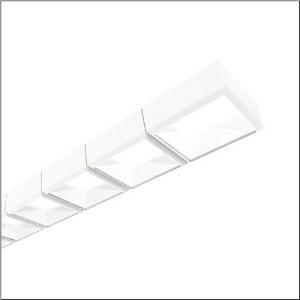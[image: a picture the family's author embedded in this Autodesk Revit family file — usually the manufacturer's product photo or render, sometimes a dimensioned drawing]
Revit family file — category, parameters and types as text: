
# Revit family: scriptus_r__11_5mz223d04wa_758a
name_source: partatom
category: Lighting Fixtures
units: mm (PartAtom-declared; Revit-internal decimal feet)

## family parameters
Cut with Voids When Loaded = No
Host = Face
Light Source = No
Part Type = Normal
Room Calculation Point = No
Round Connector Dimension = Use Diameter
Shared = No

## types (1)
- --- (1 x LED 4000K / CRI = 80 (unbekannt), 7230 lm, 4000K)
    Apparent Load = 51 VA
    CIE Flux Codes = 82 95 99 100 100
    Color Rendering = 80
    Color Temperature = 4000K
    Default Elevation = 1800 mm
    Description = Scriptus® 11, office luminaire, primary optical cover: lenses, CAT 2 (L<= 3000cd/m²), light emission: direct distribution, primary light characteristic: symmetric, installation type: surface-mounted, LED rated luminous flux: 7.230 lm, light colour: 840, colour temperature: 4000K, control gear: ECG DALI, with terminal, 5-pole, mains connection: 230V, AC, 50Hz, rated input power: 51W, housing, luminaire housing, of aluminium, traffic white (RAL 9016), length: 2.426 mm, width: 114 mm, height: 57mm, protection rating (complete): IP20, insulation class (complete): insulation class I (protective earthing), certification: CE, ENEC, VDE, protection symbol: F, permissible ambient temperature for indoor applications: 0..+35°C, standard: EN 50419, packaging unit: 1 piece
    Height = 57 mm
    Lamp = 1 x LED 4000K / CRI >= 80 (unbekannt)
    Lamp Light Flux = 7230 lm
    Lamp count = 1
    Length = 2426 mm
    Luminous efficacy = 143 lm/W
    Manufacturer = Siteco
    ModVariant = No
    Model = 5MZ223D04WA
    Mounting Place = Ceiling
    Mounting Type = Surface mounted
    Number of Poles = 1
    OnlyDefault = Yes
    Power Factor = 1
    Product Name = Scriptus® 11
    Product group = office luminaire | ceiling mounted
    ProductGroupID = 302
    Protection Class = Protection class I
    Protection Degree = IP 20
    RLX_Detail_Level = 1
    RlxData = <blob elided: 31293 chars, md5=bc968398>
    Socket = socket
    Standby Power = 0 W
    System Light Flux = 7230 lm
    System Power = 51 W
    Type Comments = factory setting: luminous flux: 100 % | dim-lin: 254 | 525 mA
    Type Image = l_1004833.jpg
    URL = http://relux.com
    VarID = @adj_146517
    Voltage = 0 V
    Weight = 0.00 kg
    Width = 114 mm

## geometry (parser evidence)
native form markers: Blend x4, Sweep x9
no freeform markers — native parametric forms only
